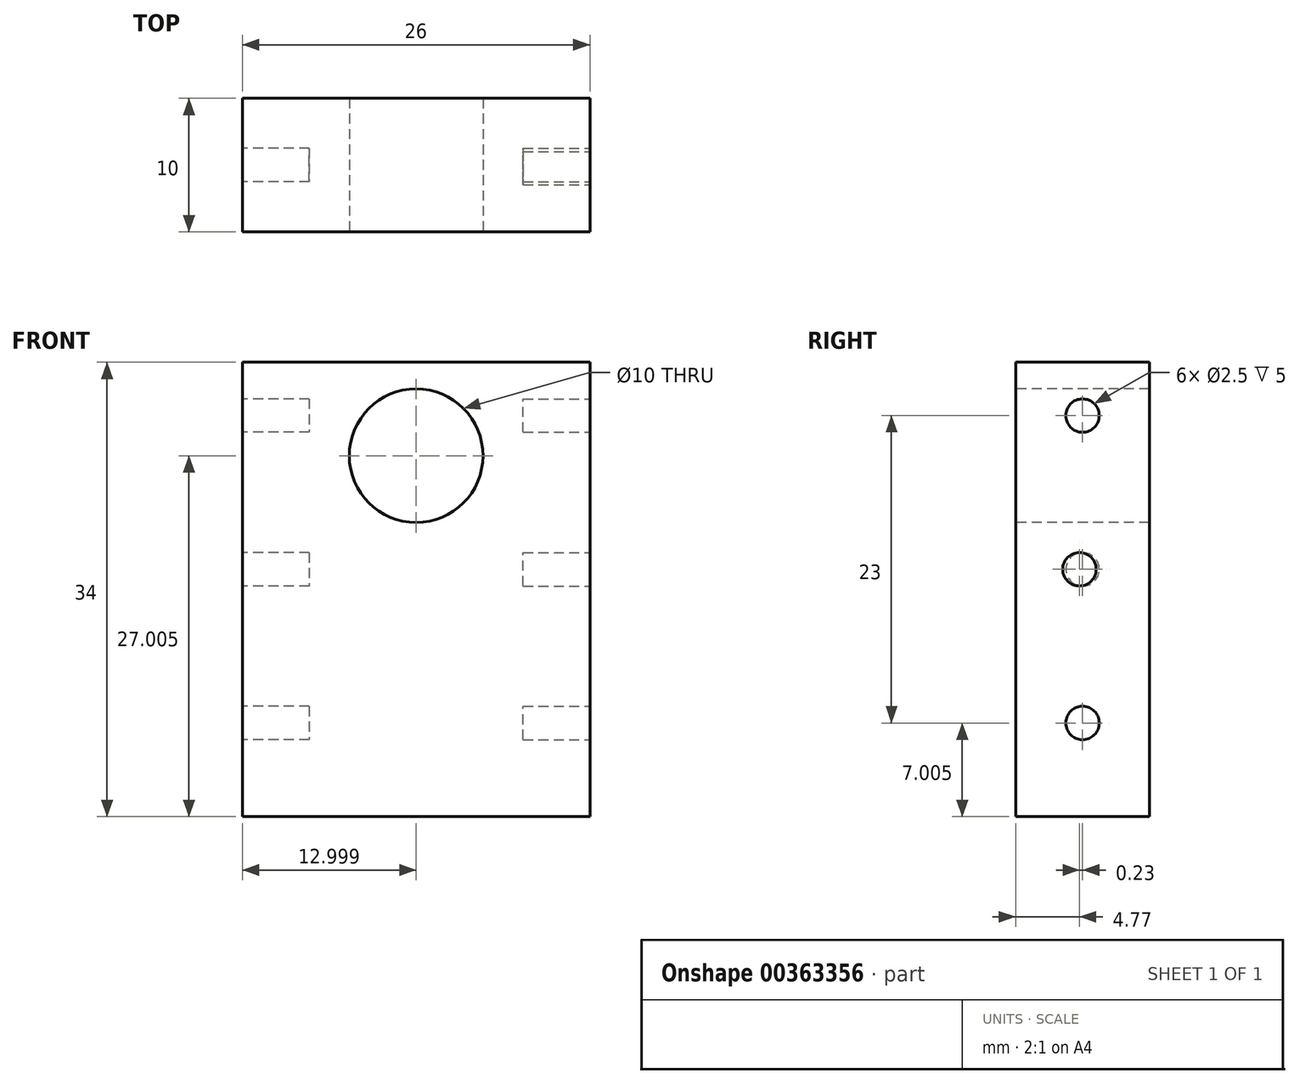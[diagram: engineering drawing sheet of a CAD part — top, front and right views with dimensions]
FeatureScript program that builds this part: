
annotation { "Feature Type Name" : "Feature", "Feature Type Description" : "" }
export const myFeature = defineFeature(function(context is Context, id is Id, definition is map)
    precondition{}
    {
        {
            var Q0;
            Q0=qCreatedBy(makeId("Front.planeOp"),FACE);
            var sketch = newSketch(context, id + "F0", { "sketchPlane" : qUnion([Q0])});
            skLineSegment(sketch, "E0.bottom", {"start": v(-51.61, 15.82) * mm, "end": v(-25.61, 15.82) * mm});
            skLineSegment(sketch, "E0.top", {"start": v(-51.61, -18.18) * mm, "end": v(-25.61, -18.18) * mm});
            skLineSegment(sketch, "E0.left", {"start": v(-51.61, 15.82) * mm, "end": v(-51.61, -18.18) * mm});
            skLineSegment(sketch, "E0.right", {"start": v(-25.61, 15.82) * mm, "end": v(-25.61, -18.18) * mm});
            skCircle(sketch, "E1", {"center": v(-38.61, 8.82) * mm, "radius": 5 * mm});
            skSolve(sketch);
        }
        {
            var Q0;
            Q0=makeQuery(id+"F0.imprint","IMPRINT",FACE,{"disambiguationData":[TD([[makeQuery(id+"F0.imprint","IMPRINT",EDGE,{"derivedFrom":sQuery(id+"F0.wireOp",EDGE,"E0.bottom")}),-1.0]])]});
            extrude(context, id + "F1", {"entities" : qUnion([Q0]), "oppositeDirection" : true, "depth" : 10 * mm});
        }
        {
            var Q0;
            Q0=makeQuery(id+"F1.opExtrude","SWEPT_FACE",FACE,{"disambiguationData":[OSD([sQuery(id+"F0.wireOp",EDGE,"E0.right")])]});
            var sketch = newSketch(context, id + "F2", { "sketchPlane" : qUnion([Q0])});
            skCircle(sketch, "E2", {"center": v(4.77, 0.32) * mm, "radius": 1.25 * mm});
            skCircle(sketch, "E3", {"center": v(5, 11.82) * mm, "radius": 1.25 * mm});
            skCircle(sketch, "E4", {"center": v(5, -11.18) * mm, "radius": 1.25 * mm});
            skSolve(sketch);
        }
        {
            var Q0;
            Q0 = qSketchRegion(id + "F2", true);
            extrude(context, id + "F3", {"entities" : qUnion([Q0]), "operationType" : NewBodyOperationType.REMOVE, "oppositeDirection" : true, "depth" : 5 * mm});
        }
        {
            var Q0;
            Q0=makeQuery(id+"F1.opExtrude","SWEPT_FACE",FACE,{"disambiguationData":[OSD([sQuery(id+"F0.wireOp",EDGE,"E0.left")])]});
            var sketch = newSketch(context, id + "F4", { "sketchPlane" : qUnion([Q0])});
            skCircle(sketch, "E5", {"center": v(-5, 11.82) * mm, "radius": 1.25 * mm});
            skCircle(sketch, "E6", {"center": v(-5, 0.32) * mm, "radius": 1.25 * mm});
            skCircle(sketch, "E7", {"center": v(-5, -11.18) * mm, "radius": 1.25 * mm});
            skSolve(sketch);
        }
        {
            var Q0;
            Q0 = qSketchRegion(id + "F4", true);
            extrude(context, id + "F5", {"entities" : qUnion([Q0]), "operationType" : NewBodyOperationType.REMOVE, "oppositeDirection" : true, "depth" : 5 * mm});
        }
    });
